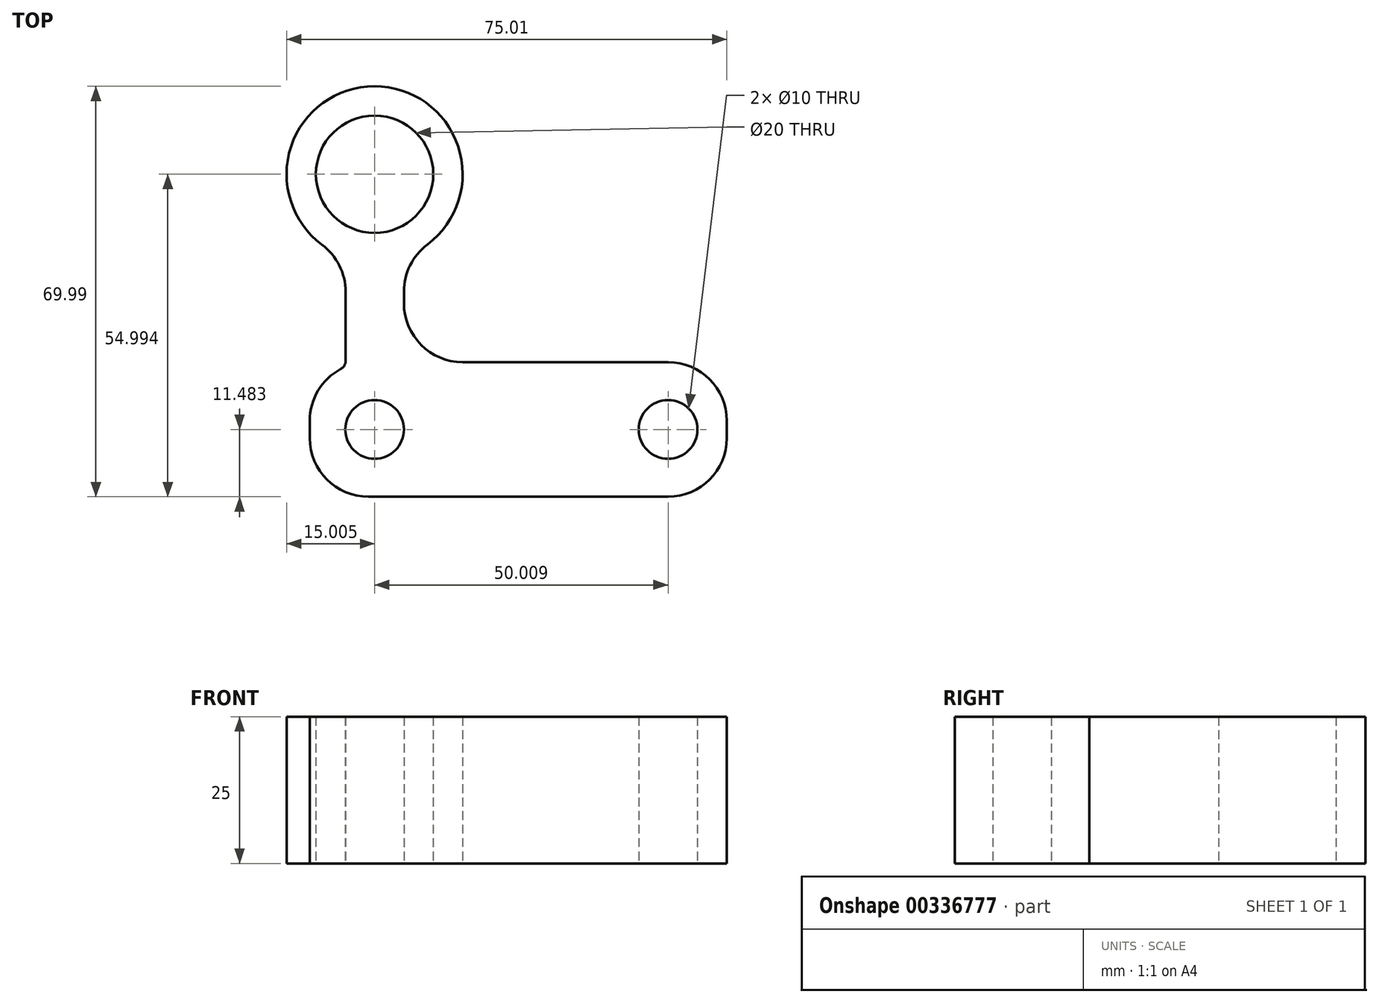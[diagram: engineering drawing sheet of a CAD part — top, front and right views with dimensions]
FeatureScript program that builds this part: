
annotation { "Feature Type Name" : "Feature", "Feature Type Description" : "" }
export const myFeature = defineFeature(function(context is Context, id is Id, definition is map)
    precondition{}
    {
        {
            var Q0;
            Q0=qCreatedBy(makeId("Top.planeOp"),FACE);
            var sketch = newSketch(context, id + "F0", { "sketchPlane" : qUnion([Q0])});
            skPoint(sketch, "E0.left.start.orphan", {"position": v(-57.06, -9.5) * mm});
            skLineSegment(sketch, "E1", {"start": v(-35.82, -5.25) * mm, "end": v(-3.39, -5.25) * mm});
            skPoint(sketch, "E2.orphan", {"position": v(6.79, -16.73) * mm});
            skPoint(sketch, "E3.visualSharp", {"position": v(11.95, -5.25) * mm});
            skPoint(sketch, "E4.visualSharp", {"position": v(1.62, -28.2) * mm});
            skPoint(sketch, "E5.visualSharp", {"position": v(-64.54, 1.98) * mm});
            skPoint(sketch, "E0.top.start.orphan", {"position": v(-57.06, -20.98) * mm});
            skLineSegment(sketch, "E6", {"start": v(-54.45, -28.2) * mm, "end": v(-3.39, -28.2) * mm});
            skPoint(sketch, "E7.visualSharp", {"position": v(-64.45, -28.2) * mm});
            skArc(sketch, "E7.filletArc", {"start": v(-64.45, -18.2) * mm, "mid": v(-61.52, -25.28) * mm, "end": v(-54.45, -28.2) * mm});
            skPoint(sketch, "E8.orphan", {"position": v(-57.06, 1.98) * mm});
            skLineSegment(sketch, "E9", {"start": v(-35.82, -5.25) * mm, "end": v(-38.4, -5.25) * mm});
            skLineSegment(sketch, "E10", {"start": v(-64.45, -15.25) * mm, "end": v(-64.45, -18.2) * mm});
            skPoint(sketch, "E11.visualSharp", {"position": v(-64.45, -5.25) * mm});
            skArc(sketch, "E11.filletArc", {"start": v(-59.16, -6.43) * mm, "mid": v(-63.03, -10.1) * mm, "end": v(-64.45, -15.25) * mm});
            skCircle(sketch, "E12", {"center": v(-53.4, -16.73) * mm, "radius": 5 * mm});
            skLineSegment(sketch, "E13", {"start": v(-53.4, 6.98) * mm, "end": v(-53.36, 6.98) * mm});
            skPoint(sketch, "E14", {"position": v(-53.36, 6.98) * mm});
            skPoint(sketch, "E15.orphan", {"position": v(-58.33, 6.98) * mm});
            skPoint(sketch, "E16.orphan", {"position": v(-48.4, 6.98) * mm});
            skLineSegment(sketch, "E17", {"start": v(-53.36, 6.98) * mm, "end": v(-53.4, 6.98) * mm});
            skLineSegment(sketch, "E18", {"start": v(-58.33, 6.98) * mm, "end": v(-58.33, -5.05) * mm});
            skLineSegment(sketch, "E19", {"start": v(-48.4, 6.98) * mm, "end": v(-48.4, 4.75) * mm});
            skCircle(sketch, "E20", {"center": v(-53.4, 26.78) * mm, "radius": 10 * mm});
            skArc(sketch, "E21", {"start": v(-44.4, 14.78) * mm, "mid": v(-53.42, 41.78) * mm, "end": v(-62.36, 14.76) * mm});
            skPoint(sketch, "E22.orphan", {"position": v(-64.45, -16.73) * mm});
            skLineSegment(sketch, "E23", {"start": v(-58.33, 6.74) * mm, "end": v(-58.33, 6.98) * mm});
            skLineSegment(sketch, "E24", {"start": v(-48.4, 6.78) * mm, "end": v(-48.4, 6.98) * mm});
            skPoint(sketch, "E25.visualSharp", {"position": v(-48.4, 12.64) * mm});
            skArc(sketch, "E25.filletArc", {"start": v(-47.48, 13) * mm, "mid": v(-48.15, 12.44) * mm, "end": v(-48.4, 11.61) * mm});
            skPoint(sketch, "E26.visualSharp", {"position": v(-58.33, 12.62) * mm});
            skArc(sketch, "E26.filletArc", {"start": v(-58.33, 11.57) * mm, "mid": v(-58.59, 12.41) * mm, "end": v(-59.27, 12.98) * mm});
            skArc(sketch, "E27.filletArc", {"start": v(-44.4, 14.78) * mm, "mid": v(-47.34, 11.26) * mm, "end": v(-48.4, 6.78) * mm});
            skArc(sketch, "E28.filletArc", {"start": v(-58.33, 6.74) * mm, "mid": v(-59.4, 11.22) * mm, "end": v(-62.36, 14.76) * mm});
            skPoint(sketch, "E29.visualSharp", {"position": v(-58.33, -6.03) * mm});
            skArc(sketch, "E29.filletArc", {"start": v(-59.16, -6.43) * mm, "mid": v(-58.56, -5.85) * mm, "end": v(-58.33, -5.05) * mm});
            skPoint(sketch, "E30.visualSharp", {"position": v(-48.4, -5.25) * mm});
            skArc(sketch, "E30.filletArc", {"start": v(-48.4, 4.75) * mm, "mid": v(-45.47, -2.32) * mm, "end": v(-38.4, -5.25) * mm});
            skPoint(sketch, "E0.right.end.orphan", {"position": v(5.55, -19.47) * mm});
            skLineSegment(sketch, "E31", {"start": v(6.61, -15.25) * mm, "end": v(6.61, -18.2) * mm});
            skPoint(sketch, "E32.visualSharp", {"position": v(6.61, -5.25) * mm});
            skArc(sketch, "E32.filletArc", {"start": v(6.61, -15.25) * mm, "mid": v(3.68, -8.18) * mm, "end": v(-3.39, -5.25) * mm});
            skPoint(sketch, "E33.visualSharp", {"position": v(6.61, -28.2) * mm});
            skArc(sketch, "E33.filletArc", {"start": v(-3.39, -28.2) * mm, "mid": v(3.68, -25.28) * mm, "end": v(6.61, -18.2) * mm});
            skCircle(sketch, "E34", {"center": v(-3.39, -16.73) * mm, "radius": 5 * mm});
            skLineSegment(sketch, "E35.trimOffspring", {"start": v(6.61, -16.73) * mm, "end": v(6.79, -16.73) * mm});
            skSolve(sketch);
        }
        {
            var Q0;
            Q0 = qSketchRegion(id + "F0", true);
            extrude(context, id + "F1", {"entities" : qUnion([Q0]), "depth" : 25 * mm});
        }
        {
            var Q0;
            Q0 = qSketchRegion(id + "F0", true);
            extrude(context, id + "F2", {"entities" : qUnion([Q0]), "operationType" : NewBodyOperationType.ADD, "depth" : 25 * mm});
        }
    });
